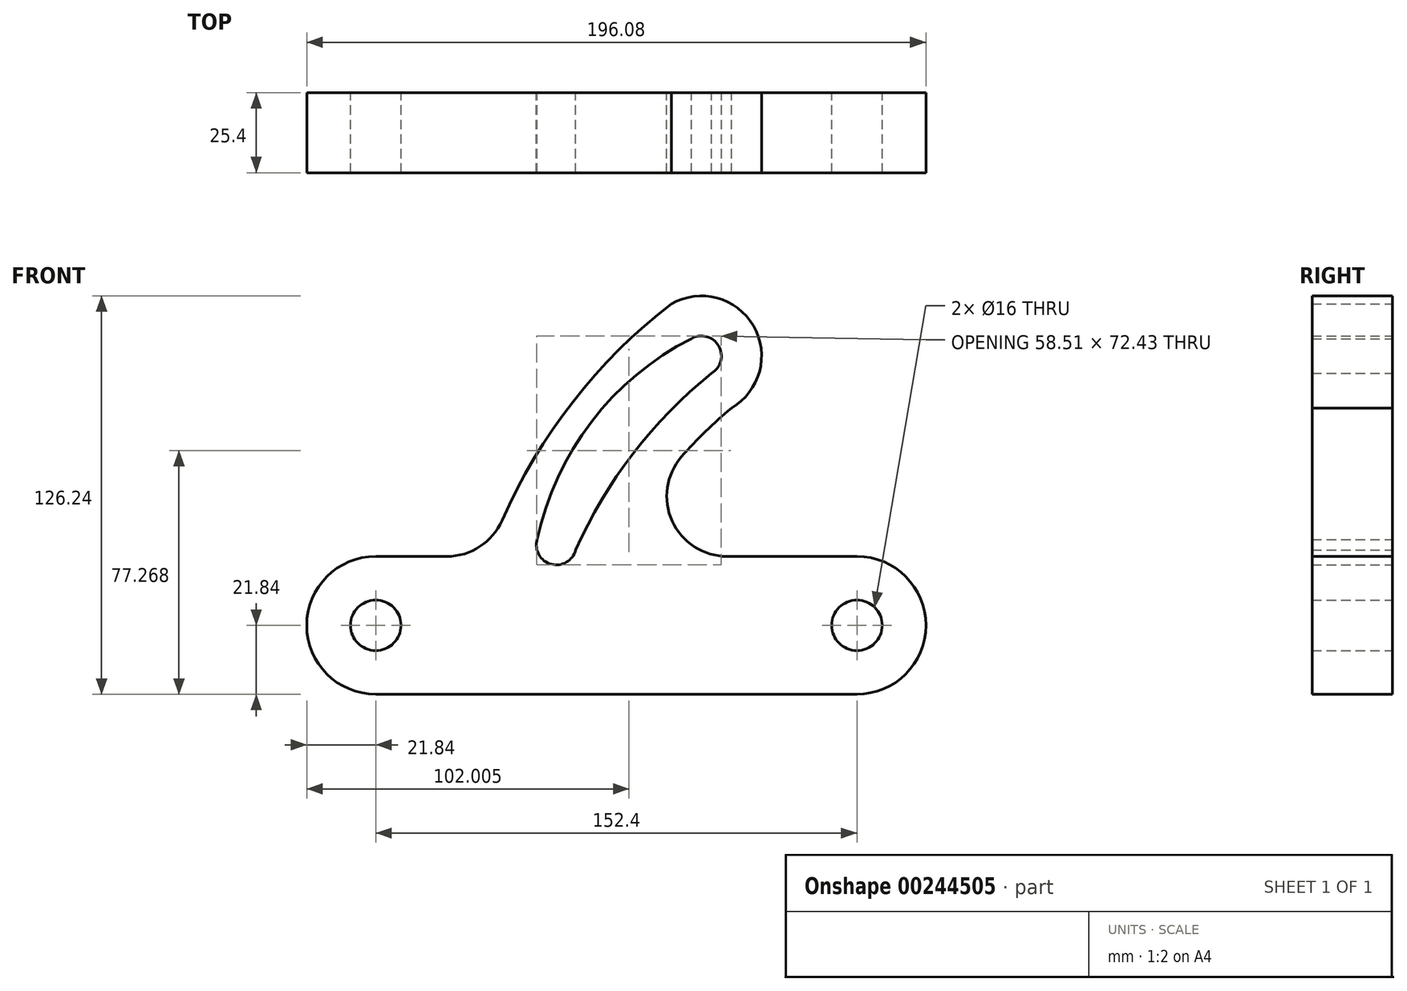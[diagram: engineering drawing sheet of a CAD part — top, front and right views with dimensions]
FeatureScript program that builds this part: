
annotation { "Feature Type Name" : "Feature", "Feature Type Description" : "" }
export const myFeature = defineFeature(function(context is Context, id is Id, definition is map)
    precondition{}
    {
        {
            var Q0;
            Q0=qCreatedBy(makeId("Front.planeOp"),FACE);
            var sketch = newSketch(context, id + "F0", { "sketchPlane" : qUnion([Q0])});
            skCircle(sketch, "E0", {"center": v(0, 0) * mm, "radius": 8 * mm});
            skLineSegment(sketch, "E1", {"start": v(0, 0) * mm, "end": v(-152.4, 0) * mm, "construction": true});
            skArc(sketch, "E2", {"start": v(0, -21.84) * mm, "mid": v(21.84, 0) * mm, "end": v(0, 21.84) * mm});
            skLineSegment(sketch, "E3", {"start": v(-76.2, -37.44) * mm, "end": v(-76.2, 47.05) * mm, "construction": true});
            skPoint(sketch, "E3.startSnap0", {"position": v(-76.2, 0) * mm});
            skLineSegment(sketch, "E4", {"start": v(0, 21.84) * mm, "end": v(-41.18, 21.84) * mm});
            skLineSegment(sketch, "E5", {"start": v(0, -21.84) * mm, "end": v(-76.2, -21.84) * mm});
            skLineSegment(sketch, "E6.MirrorCS", {"start": v(-152.4, 21.84) * mm, "end": v(-129.84, 21.84) * mm});
            skArc(sketch, "E7.MirrorCS", {"start": v(-152.4, -21.84) * mm, "mid": v(-174.24, 0) * mm, "end": v(-152.4, 21.84) * mm});
            skCircle(sketch, "E8.MirrorC", {"center": v(-152.4, 0) * mm, "radius": 8 * mm});
            skLineSegment(sketch, "E9.MirrorCS", {"start": v(-152.4, -21.84) * mm, "end": v(-76.2, -21.84) * mm});
            skCircle(sketch, "E10", {"center": v(0, 0) * mm, "radius": 98.55 * mm, "construction": true});
            skLineSegment(sketch, "E11", {"start": v(0, 0) * mm, "end": v(0, 188.3) * mm, "construction": true});
            skLineSegment(sketch, "E12", {"start": v(0, 0) * mm, "end": v(-174.24, 301.8) * mm, "construction": true});
            skPoint(sketch, "E12.endSnap0", {"position": v(-174.24, 0) * mm});
            skLineSegment(sketch, "E13", {"start": v(0, 0) * mm, "end": v(-191.03, 51.19) * mm, "construction": true});
            skArc(sketch, "E14", {"start": v(-46.1, 79.85) * mm, "mid": v(-43.78, 88.52) * mm, "end": v(-52.45, 90.85) * mm});
            skArc(sketch, "E15", {"start": v(-101.33, 27.15) * mm, "mid": v(-96.84, 19.37) * mm, "end": v(-89.06, 23.86) * mm});
            skArc(sketch, "E16", {"start": v(-52.45, 90.85) * mm, "mid": v(-84.08, 64.52) * mm, "end": v(-101.33, 27.15) * mm});
            skArc(sketch, "E17", {"start": v(-46.1, 79.85) * mm, "mid": v(-70.9, 54.4) * mm, "end": v(-89.06, 23.86) * mm});
            skArc(sketch, "E18", {"start": v(-39.75, 68.85) * mm, "mid": v(-32.78, 94.87) * mm, "end": v(-58.8, 101.85) * mm});
            skArc(sketch, "E19", {"start": v(-39.75, 68.85) * mm, "mid": v(-47.96, 61.44) * mm, "end": v(-55.54, 53.4) * mm});
            skArc(sketch, "E20", {"start": v(-58.8, 101.85) * mm, "mid": v(-89.9, 70.91) * mm, "end": v(-112.4, 33.25) * mm});
            skPoint(sketch, "E21.trimOffspring.end.orphan", {"position": v(-76.2, 21.84) * mm});
            skArc(sketch, "E22.filletArc", {"start": v(-55.54, 53.4) * mm, "mid": v(-58.51, 33) * mm, "end": v(-41.18, 21.84) * mm});
            skPoint(sketch, "E23.visualSharp", {"position": v(-116.92, 21.84) * mm});
            skArc(sketch, "E23.filletArc", {"start": v(-129.84, 21.84) * mm, "mid": v(-119.42, 24.95) * mm, "end": v(-112.4, 33.25) * mm});
            skSolve(sketch);
        }
        {
            var Q0;
            Q0 = qSketchRegion(id + "F0", true);
            extrude(context, id + "F1", {"entities" : qUnion([Q0]), "depth" : 25.4 * mm});
        }
    });
